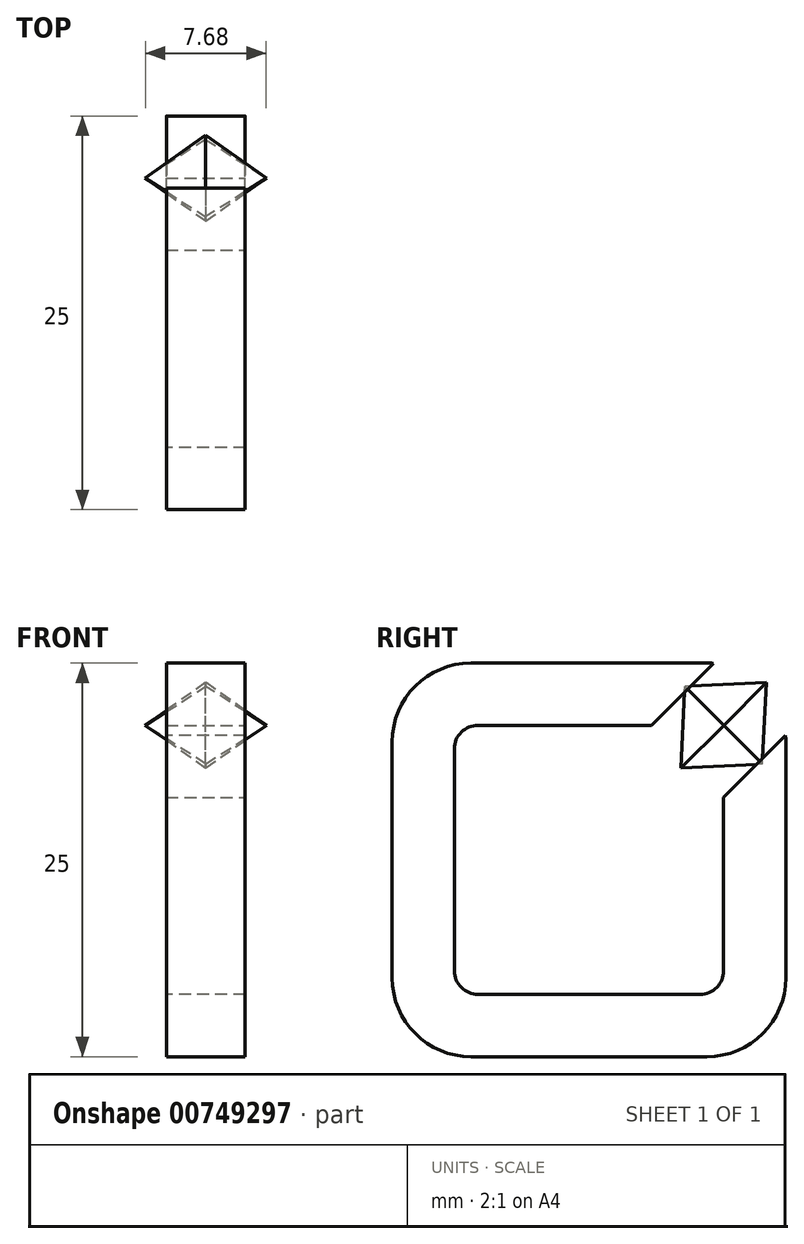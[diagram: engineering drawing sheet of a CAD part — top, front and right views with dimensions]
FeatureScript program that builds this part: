
annotation { "Feature Type Name" : "Feature", "Feature Type Description" : "" }
export const myFeature = defineFeature(function(context is Context, id is Id, definition is map)
    precondition{}
    {
        {
            var Q0;
            Q0=qCreatedBy(makeId("Right.planeOp"),FACE);
            var sketch = newSketch(context, id + "F0", { "sketchPlane" : qUnion([Q0])});
            skLineSegment(sketch, "E0.bottom", {"start": v(8.55, 8.55) * mm, "end": v(-8.55, 8.55) * mm});
            skLineSegment(sketch, "E0.top", {"start": v(8.55, -8.55) * mm, "end": v(-8.55, -8.55) * mm});
            skLineSegment(sketch, "E0.left", {"start": v(8.55, 8.55) * mm, "end": v(8.55, -8.55) * mm});
            skLineSegment(sketch, "E0.right", {"start": v(-8.55, 8.55) * mm, "end": v(-8.55, -8.55) * mm});
            skPoint(sketch, "E0.middle", {"position": v(0, 0) * mm});
            skLineSegment(sketch, "E1.bottom", {"start": v(12.5, -12.5) * mm, "end": v(-12.5, -12.5) * mm});
            skLineSegment(sketch, "E1.top", {"start": v(12.5, 12.5) * mm, "end": v(-12.5, 12.5) * mm});
            skLineSegment(sketch, "E1.left", {"start": v(12.5, -12.5) * mm, "end": v(12.5, 12.5) * mm});
            skLineSegment(sketch, "E1.right", {"start": v(-12.5, -12.5) * mm, "end": v(-12.5, 12.5) * mm});
            skSolve(sketch);
        }
        {
            var Q0;
            Q0=makeQuery(id+"F0.imprint","IMPRINT",FACE,{"disambiguationData":[TD([[makeQuery(id+"F0.imprint","IMPRINT",EDGE,{"derivedFrom":sQuery(id+"F0.wireOp",EDGE,"E0.bottom")}),-1.0]])]});
            extrude(context, id + "F1", {"entities" : qUnion([Q0]), "endBound" : BoundingType.SYMMETRIC, "depth" : 5 * mm, "offsetDistance" : 25 * mm});
        }
        {
            var Q0;
            Q0=makeQuery(id+"F1.opExtrude","SWEPT_EDGE",EDGE,{"disambiguationData":[OSD([sQuery(id+"F0.wireOp",EDGE,"E1.top"),sQuery(id+"F0.wireOp",EDGE,"E1.right")])]});
            var Q1;
            Q1=makeQuery(id+"F1.opExtrude","SWEPT_EDGE",EDGE,{"disambiguationData":[OSD([sQuery(id+"F0.wireOp",EDGE,"E1.top"),sQuery(id+"F0.wireOp",EDGE,"E1.left")])]});
            var Q2;
            Q2=makeQuery(id+"F1.opExtrude","SWEPT_EDGE",EDGE,{"disambiguationData":[OSD([sQuery(id+"F0.wireOp",EDGE,"E1.bottom"),sQuery(id+"F0.wireOp",EDGE,"E1.left")])]});
            var Q3;
            Q3=makeQuery(id+"F1.opExtrude","SWEPT_EDGE",EDGE,{"disambiguationData":[OSD([sQuery(id+"F0.wireOp",EDGE,"E1.bottom"),sQuery(id+"F0.wireOp",EDGE,"E1.right")])]});
            fillet(context, id + "F2", {"entities" : qUnion([Q0, Q1, Q2, Q3]), "radius" : 5 * mm, "tangentPropagation" : true, "allowEdgeOverflow" : false});
        }
        {
            var Q0;
            Q0=makeQuery(id+"F1.opExtrude","SWEPT_EDGE",EDGE,{"disambiguationData":[OSD([sQuery(id+"F0.wireOp",EDGE,"E0.bottom"),sQuery(id+"F0.wireOp",EDGE,"E0.right")])]});
            var Q1;
            Q1=makeQuery(id+"F1.opExtrude","SWEPT_EDGE",EDGE,{"disambiguationData":[OSD([sQuery(id+"F0.wireOp",EDGE,"E0.bottom"),sQuery(id+"F0.wireOp",EDGE,"E0.left")])]});
            var Q2;
            Q2=makeQuery(id+"F1.opExtrude","SWEPT_EDGE",EDGE,{"disambiguationData":[OSD([sQuery(id+"F0.wireOp",EDGE,"E0.top"),sQuery(id+"F0.wireOp",EDGE,"E0.right")])]});
            var Q3;
            Q3=makeQuery(id+"F1.opExtrude","SWEPT_EDGE",EDGE,{"disambiguationData":[OSD([sQuery(id+"F0.wireOp",EDGE,"E0.top"),sQuery(id+"F0.wireOp",EDGE,"E0.left")])]});
            fillet(context, id + "F3", {"entities" : qUnion([Q0, Q1, Q2, Q3]), "radius" : 1.5 * mm, "tangentPropagation" : true, "allowEdgeOverflow" : false});
        }
        {
            var Q0;
            Q0=makeQuery(id+"F1.opExtrude","CAP_FACE",FACE,{"disambiguationData":[OSD([sQuery(id+"F0.wireOp",EDGE,"E0.bottom"),sQuery(id+"F0.wireOp",EDGE,"E0.top"),sQuery(id+"F0.wireOp",EDGE,"E0.left"),sQuery(id+"F0.wireOp",EDGE,"E0.right"),sQuery(id+"F0.wireOp",EDGE,"E1.bottom"),sQuery(id+"F0.wireOp",EDGE,"E1.top"),sQuery(id+"F0.wireOp",EDGE,"E1.left"),sQuery(id+"F0.wireOp",EDGE,"E1.right")])],"isStart":false});
            var sketch = newSketch(context, id + "F4", { "sketchPlane" : qUnion([Q0])});
            skLineSegment(sketch, "E2", {"start": v(2.47, 7.05) * mm, "end": v(13.93, 18.5) * mm});
            skLineSegment(sketch, "E3", {"start": v(13.93, 18.5) * mm, "end": v(18.5, 13.93) * mm});
            skLineSegment(sketch, "E4", {"start": v(18.5, 13.93) * mm, "end": v(7.05, 2.47) * mm});
            skLineSegment(sketch, "E5", {"start": v(7.05, 2.47) * mm, "end": v(2.47, 7.05) * mm});
            skLineSegment(sketch, "E6", {"start": v(16.22, 16.22) * mm, "end": v(0, 0) * mm, "construction": true});
            skPoint(sketch, "E6.startSnap0", {"position": v(16.22, 16.22) * mm});
            skLineSegment(sketch, "E7", {"start": v(0, 0) * mm, "end": v(8.11, 8.11) * mm, "construction": true});
            skSolve(sketch);
        }
        {
            var Q0;
            Q0 = qSketchRegion(id + "F4", true);
            extrude(context, id + "F5", {"entities" : qUnion([Q0]), "operationType" : NewBodyOperationType.REMOVE, "oppositeDirection" : true, "depth" : 25 * mm, "offsetDistance" : 25 * mm});
        }
        {
            var Q0;
            Q0=makeQuery(id+"F5.boolean.opBoolean","COPY",FACE,{"derivedFrom":makeQuery(id+"F5.opExtrude","SWEPT_FACE",FACE,{"disambiguationData":[OSD([sQuery(id+"F4.wireOp",EDGE,"E2")])]})});
            cPlane(context, id + "F6", {"entities" : qUnion([Q0]), "cplaneType" : CPlaneType.OFFSET, "offset" : (6.47 / 2) * mm, "width" : 150 * mm, "height" : 150 * mm});
        }
        {
            var Q0;
            Q0=qCreatedBy(id+"F6.planeOp",FACE);
            var sketch = newSketch(context, id + "F7", { "sketchPlane" : qUnion([Q0])});
            skCircle(sketch, "E8.cCircle", {"center": v(0, 12.1) * mm, "radius": 2.72 * mm, "construction": true});
            skLineSegment(sketch, "E8.0", {"start": v(0, 15.94) * mm, "end": v(3.84, 12.1) * mm});
            skLineSegment(sketch, "E8.1", {"start": v(3.84, 12.1) * mm, "end": v(0, 8.25) * mm});
            skLineSegment(sketch, "E8.2", {"start": v(0, 8.25) * mm, "end": v(-3.84, 12.1) * mm});
            skLineSegment(sketch, "E8.3", {"start": v(-3.84, 12.1) * mm, "end": v(0, 15.94) * mm});
            skPoint(sketch, "E8.0.midPoint", {"position": v(1.92, 14.02) * mm});
            skSolve(sketch);
        }
        {
            var Q0;
            Q0 = qSketchRegion(id + "F7", true);
            extrude(context, id + "F8", {"entities" : qUnion([Q0]), "depth" : 25 * mm, "offsetDistance" : 25 * mm, "hasDraft" : true, "draftAngle" : 38 * degree, "draftPullDirection" : true, "hasSecondDirection" : true, "secondDirectionOppositeDirection" : true, "secondDirectionDepth" : 50 * mm, "hasSecondDirectionDraft" : true, "secondDirectionDraftAngle" : 38 * degree, "secondDirectionDraftPullDirection" : true});
        }
    });
